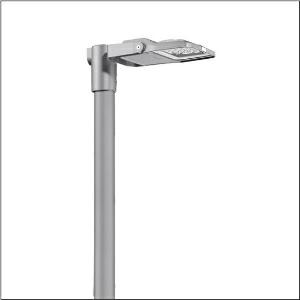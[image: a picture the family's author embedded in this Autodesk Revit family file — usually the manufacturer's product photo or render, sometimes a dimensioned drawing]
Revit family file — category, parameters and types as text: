
# Revit family: floodlight_fl_21_iq_micro___pl43_5xa7762a4a3a_9a39
name_source: partatom
category: Lighting Fixtures
units: mm (PartAtom-declared; Revit-internal decimal feet)

## family parameters
Cut with Voids When Loaded = No
Host = Face
Light Source = No
Part Type = Normal
Room Calculation Point = No
Round Connector Dimension = Use Diameter
Shared = No

## types (1)
- --- (1 x LED, 3170 lm, 23.1 W, 4000K)
    Apparent Load = 23 VA
    CIE Flux Codes = 29 80 99 100 100
    Color Rendering = 70
    Color Temperature = 4000K
    Default Elevation = 1800 mm
    Description = Floodlight FL 21 iQ micro, floodlight, primary light control with lens, of PMMA, primary optical cover: protective disc, of toughened safety glass, transparent, light distribution: PL43, light emission: direct distribution, installation type: surface-mounted, LED, High Power LED, rated luminous flux: 3.170lm, luminous efficacy: 137lm/W, light colour: 740, colour temperature: 4000K, control: Auto-Match, Temp-Guard, Night-Set, Smart-Wire, Desk-Remote (wireless, voltage-free reading and setting of iQ features in the workshop via application-optimized NFC function/RFID function), optimised constant luminous flux control (CLO 2.0), Street-Remote, with terminal, 6-pole, mains connection: 220..240V, AC, 50/60Hz, start of lifetime: 23W, end of service life: 24W, reduction: 11W, luminaire housing, of diecast aluminium, powder-coated, Siteco® metallic grey (DB 702S), corrosivity category C5 mid according to DIN EN ISO 12944, sealing non-destructively replaceable, please order mast flange separately, mast bracket, of steel, galvanised, powder-coated, Siteco® metallic grey (DB 702S), protection rating (complete): IP66, insulation class (complete): insulation class II (safety insulation), certification: CE, ENEC, VDE, protection symbol: D, impact resistance: IK07, permissible operating ambient temperature: -40..+40°C, permissible operating ambient temperature for outdoor applications: -40..+50°C, standard: DIN EN 12944, LABS conformity tested according to VDMA 24364:2018-05, packaging unit: 1 piece

Light Distribution: PL43
    Height = 65 mm
    Lamp = 1 x LED
    Lamp Light Flux = 3170 lm
    Lamp Power = 23.1 W
    Lamp count = 1
    Length = 312 mm
    Luminous efficacy = 137 lm/W
    Manufacturer = Siteco
    ModVariant = No
    Model = 5XA7762A4A3A
    Number of Poles = 1
    OnlyDefault = Yes
    Power Factor = 1
    Product Name = Floodlight FL 21 iQ micro | PL43
    Product group = floodlight | pylon annexe
    ProductGroupID = 6200
    Protection Class = Protection class II
    Protection Degree = IP 66
    RLX_Detail_Level = 1
    RLX_Emergency_Light_Flux = 0 lm
    RLX_Emergency_Type = 0
    RLX_Emergency_Type_DB = No
    RlxData = <blob elided: 101633 chars, md5=f3fe3afb>
    Socket = socket
    Standby Power = 0 W
    System Light Flux = 3170 lm
    System Power = 23 W
    Type Comments = factory setting: luminous flux: 100 % | dim-lin: 254 | 455 mA
    Type Image = l_1007121.jpg
    URL = http://relux.com
    VarID = @adj_127631
    Voltage = 0 V
    Weight = 0.00 kg
    Width = 230 mm

## geometry (parser evidence)
native form markers: Blend x4, Sweep x12
no freeform markers — native parametric forms only
